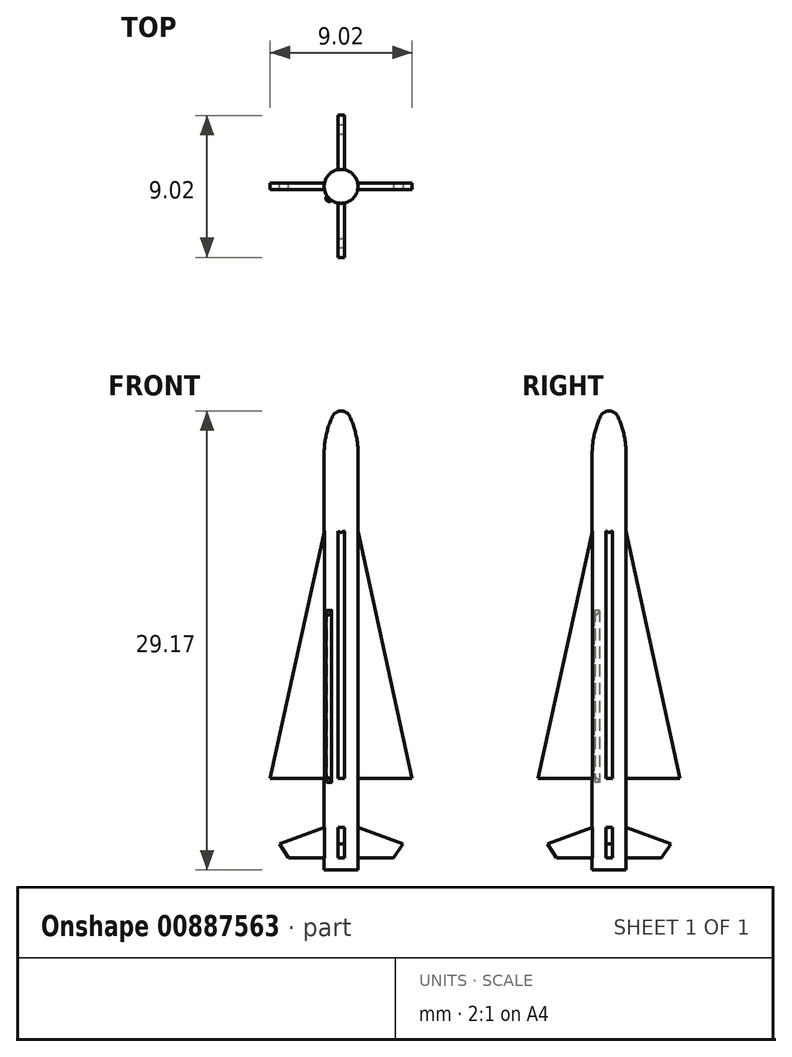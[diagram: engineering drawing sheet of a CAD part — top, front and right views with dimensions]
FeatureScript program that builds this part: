
annotation { "Feature Type Name" : "Feature", "Feature Type Description" : "" }
export const myFeature = defineFeature(function(context is Context, id is Id, definition is map)
    precondition{}
    {
        {
            var Q0;
            Q0=qCreatedBy(makeId("Front.planeOp"),FACE);
            var sketch = newSketch(context, id + "F0", { "sketchPlane" : qUnion([Q0])});
            skLineSegment(sketch, "E0", {"start": v(0, 0) * mm, "end": v(0, 29.17) * mm});
            skLineSegment(sketch, "E1", {"start": v(1.08, 26.46) * mm, "end": v(1.08, 0) * mm});
            skLineSegment(sketch, "E2", {"start": v(1.08, 0) * mm, "end": v(0, 0) * mm});
            skArc(sketch, "E3", {"start": v(0.55, 28.82) * mm, "mid": v(0.32, 29.07) * mm, "end": v(0, 29.17) * mm});
            skArc(sketch, "E4", {"start": v(1.08, 26.46) * mm, "mid": v(0.94, 27.67) * mm, "end": v(0.55, 28.82) * mm});
            skLineSegment(sketch, "E5", {"start": v(0, 29.17) * mm, "end": v(707.3, 29.17) * mm, "construction": true});
            skSolve(sketch);
        }
        {
            var Q0;
            Q0=makeQuery(id+"F0.imprint","IMPRINT",FACE,{"disambiguationData":[TD([[makeQuery(id+"F0.imprint","IMPRINT",EDGE,{"derivedFrom":sQuery(id+"F0.wireOp",EDGE,"E0")}),-1.0]])]});
            var Q1;
            Q1=sQuery(id+"F0.wireOp",EDGE,"E0");
            revolve(context, id + "F1", {"surfaceOperationType" : NewSurfaceOperationType.NEW, "entities" : qUnion([Q0]), "axis" : qUnion([Q1]), "revolveType" : RevolveType.FULL});
        }
        {
            var Q0;
            Q0=qCreatedBy(makeId("Front.planeOp"),FACE);
            var sketch = newSketch(context, id + "F2", { "sketchPlane" : qUnion([Q0])});
            skLineSegment(sketch, "E6.0", {"start": v(1.08, 26.46) * mm, "end": v(-1.08, 26.46) * mm, "construction": true});
            skLineSegment(sketch, "E7", {"start": v(0, 0.76) * mm, "end": v(3.33, 0.76) * mm});
            skLineSegment(sketch, "E8", {"start": v(3.92, 1.67) * mm, "end": v(1.08, 2.7) * mm});
            skLineSegment(sketch, "E9", {"start": v(0.4, 2.96) * mm, "end": v(0.4, 5.83) * mm});
            skLineSegment(sketch, "E10", {"start": v(0.4, 5.83) * mm, "end": v(4.51, 5.83) * mm});
            skLineSegment(sketch, "E11", {"start": v(4.51, 5.83) * mm, "end": v(0, 26.35) * mm});
            skLineSegment(sketch, "E12", {"start": v(0, 26.35) * mm, "end": v(0, 0.76) * mm});
            skLineSegment(sketch, "E13", {"start": v(1.08, 26.46) * mm, "end": v(1.08, 0) * mm, "construction": true});
            skPoint(sketch, "E14", {"position": v(1.08, 21.46) * mm});
            skLineSegment(sketch, "E15", {"start": v(1.08, 2.7) * mm, "end": v(0.4, 2.96) * mm});
            skLineSegment(sketch, "E16", {"start": v(3.33, 0.76) * mm, "end": v(3.92, 1.67) * mm});
            skSolve(sketch);
        }
        {
            var Q0;
            Q0=qSketchRegion(id+"F2",true);
            extrude(context, id + "F3", {"entities" : qUnion([Q0]), "operationType" : NewBodyOperationType.ADD, "oppositeDirection" : true, "depth" : .4 * mm, "offsetDistance" : 25 * mm, "symmetric" : true});
        }
        {
            var Q0;
            Q0=makeQuery(id+"F1.opRevolve","SWEPT_BODY",BODY,{"disambiguationData":[OSD([sQuery(id+"F0.wireOp",EDGE,"E0"),sQuery(id+"F0.wireOp",EDGE,"E1"),sQuery(id+"F0.wireOp",EDGE,"E2"),sQuery(id+"F0.wireOp",EDGE,"h1jDSi8t-veb7-85qg-XgDk-6E8DmZjBuz4r")])]});
            var Q1;
            Q1=makeQuery(id+"F1.opRevolve","SWEPT_FACE",FACE,{"disambiguationData":[OSD([sQuery(id+"F0.wireOp",EDGE,"E1")])]});
            circularPattern(context, id + "F4", {"operationType" : NewBodyOperationType.ADD, "entities" : qUnion([Q0]), "axis" : qUnion([Q1]), "angle" : 360 * degree, "instanceCount" : 4, "equalSpace" : true, "computeTransformsWithoutBuiltin" : true});
        }
        {
            var Q0;
            Q0=qCreatedBy(makeId("Top.planeOp"),FACE);
            cPlane(context, id + "F5", {"entities" : qUnion([Q0]), "cplaneType" : CPlaneType.OFFSET, "offset" : 6 * mm, "width" : 150 * mm, "height" : 150 * mm});
        }
        {
            var Q0;
            Q0=qCreatedBy(id+"F5.planeOp",FACE);
            var sketch = newSketch(context, id + "F6", { "sketchPlane" : qUnion([Q0])});
            skLineSegment(sketch, "E17", {"start": v(-0.9, -0.62) * mm, "end": v(-0.7, -0.42) * mm});
            skLineSegment(sketch, "E18", {"start": v(-0.7, -0.42) * mm, "end": v(-0.42, -0.7) * mm});
            skLineSegment(sketch, "E19", {"start": v(-0.42, -0.7) * mm, "end": v(-0.62, -0.9) * mm});
            skArc(sketch, "E20", {"start": v(-0.9, -0.62) * mm, "mid": v(-0.9, -0.9) * mm, "end": v(-0.62, -0.9) * mm});
            skLineSegment(sketch, "E21", {"start": v(-0.57, -0.57) * mm, "end": v(0, 0) * mm, "construction": true});
            skLineSegment(sketch, "E22", {"start": v(0, 0) * mm, "end": v(-0.48, 0) * mm, "construction": true});
            skSolve(sketch);
        }
        {
            var Q0;
            Q0=makeQuery(id+"F6.imprint","IMPRINT",FACE,{"disambiguationData":[TD([[makeQuery(id+"F6.imprint","IMPRINT",EDGE,{"derivedFrom":sQuery(id+"F6.wireOp",EDGE,"E17")}),-1.0]])]});
            extrude(context, id + "F7", {"entities" : qUnion([Q0]), "operationType" : NewBodyOperationType.ADD, "depth" : (1450 / 144) * mm, "offsetDistance" : 25 * mm});
        }
        {
            var Q0;
            Q0=makeQuery(id+"F7.boolean.opBoolean","INTERSECT",EDGE,{"derivedFrom":[makeQuery(id+"F1.opRevolve","SWEPT_FACE",FACE,{"disambiguationData":[OSD([sQuery(id+"F0.wireOp",EDGE,"E1")])]}),makeQuery(id+"F7.opExtrude","CAP_FACE",FACE,{"disambiguationData":[OSD([sQuery(id+"F6.wireOp",EDGE,"E17"),sQuery(id+"F6.wireOp",EDGE,"E18"),sQuery(id+"F6.wireOp",EDGE,"E19"),sQuery(id+"F6.wireOp",EDGE,"E20")])],"isStart":false})]});
            var Q1;
            Q1=makeQuery(id+"F7.boolean.opBoolean","INTERSECT",EDGE,{"derivedFrom":[makeQuery(id+"F1.opRevolve","SWEPT_FACE",FACE,{"disambiguationData":[OSD([sQuery(id+"F0.wireOp",EDGE,"E1")])]}),makeQuery(id+"F7.opExtrude","CAP_FACE",FACE,{"disambiguationData":[OSD([sQuery(id+"F6.wireOp",EDGE,"E17"),sQuery(id+"F6.wireOp",EDGE,"E18"),sQuery(id+"F6.wireOp",EDGE,"E19"),sQuery(id+"F6.wireOp",EDGE,"E20")])],"isStart":true})]});
            chamfer(context, id + "F8", {"entities" : qUnion([Q0, Q1]), "chamferType" : ChamferType.OFFSET_ANGLE, "width" : .25 * mm, "oppositeDirection" : true, "angle" : 60 * degree, "tangentPropagation" : true});
        }
    });
